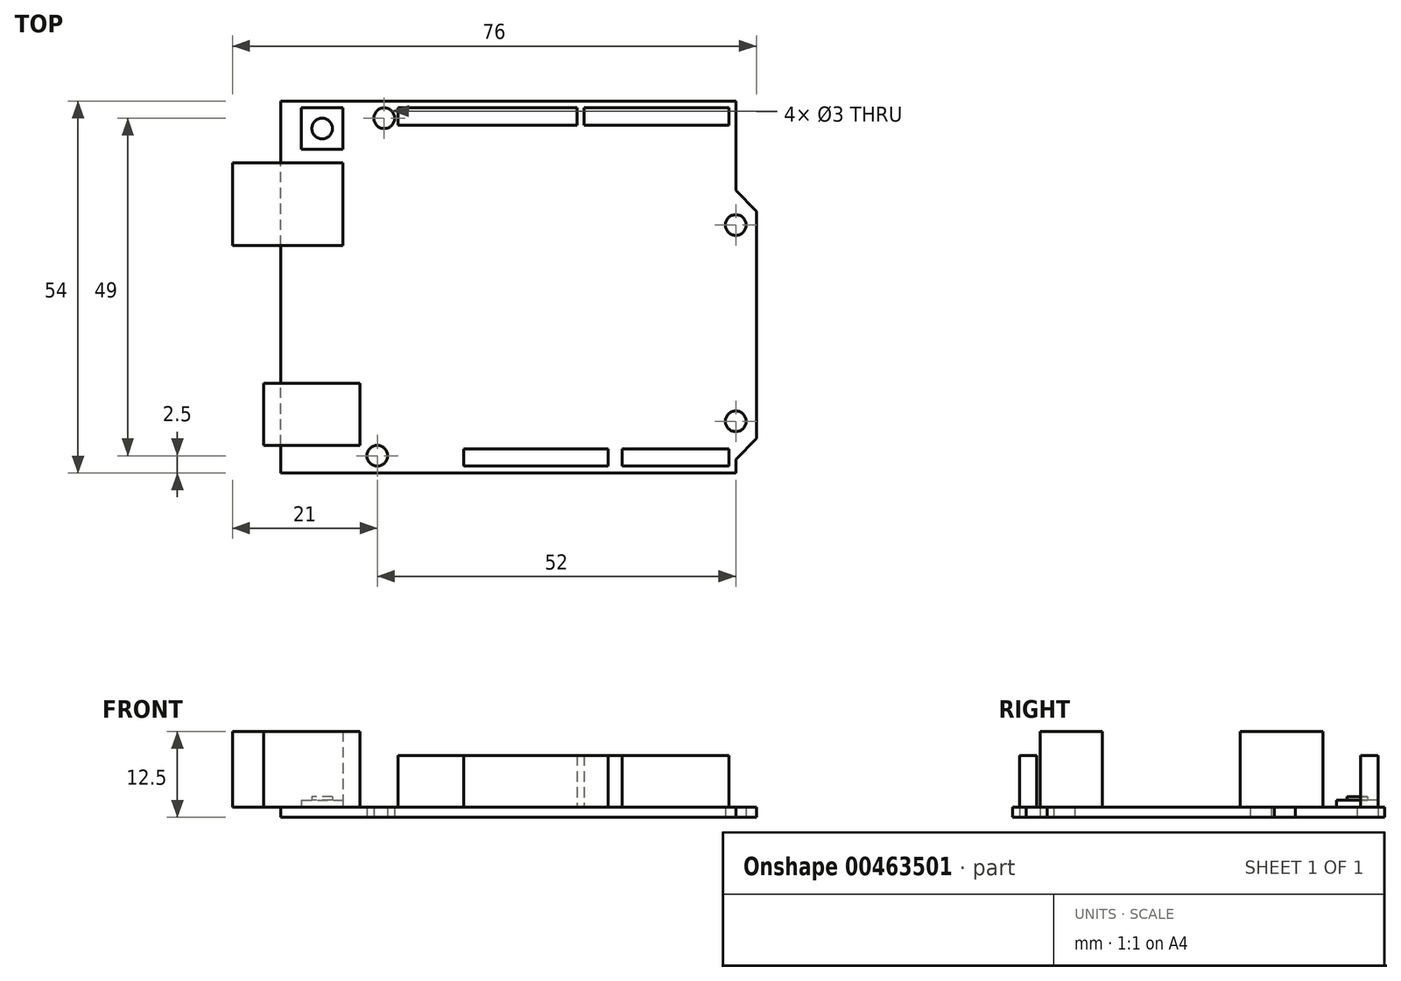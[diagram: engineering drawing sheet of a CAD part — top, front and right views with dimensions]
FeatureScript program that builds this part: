
annotation { "Feature Type Name" : "Feature", "Feature Type Description" : "" }
export const myFeature = defineFeature(function(context is Context, id is Id, definition is map)
    precondition{}
    {
        {
            var Q0;
            Q0=qCreatedBy(makeId("Top.planeOp"),FACE);
            var sketch = newSketch(context, id + "F0", { "sketchPlane" : qUnion([Q0])});
            skLineSegment(sketch, "E0.bottom", {"start": v(-33, 27) * mm, "end": v(33, 27) * mm});
            skLineSegment(sketch, "E0.top", {"start": v(-33, -27) * mm, "end": v(33, -27) * mm});
            skLineSegment(sketch, "E0.left", {"start": v(-33, 27) * mm, "end": v(-33, -27) * mm});
            skLineSegment(sketch, "E0.right", {"start": v(33, 27) * mm, "end": v(33, -27) * mm});
            skLineSegment(sketch, "E1", {"start": v(33, 14) * mm, "end": v(36, 11) * mm});
            skLineSegment(sketch, "E2", {"start": v(36, 11) * mm, "end": v(36, -22) * mm});
            skLineSegment(sketch, "E3", {"start": v(36, -22) * mm, "end": v(33, -25) * mm});
            skCircle(sketch, "E4", {"center": v(33, -19.5) * mm, "radius": 1.5 * mm});
            skCircle(sketch, "E5", {"center": v(-19, -24.5) * mm, "radius": 1.5 * mm});
            skCircle(sketch, "E6", {"center": v(-18, 24.5) * mm, "radius": 1.5 * mm});
            skCircle(sketch, "E7", {"center": v(33, 9) * mm, "radius": 1.5 * mm});
            skLineSegment(sketch, "E8.bottom", {"start": v(-40, 18) * mm, "end": v(-24, 18) * mm});
            skLineSegment(sketch, "E8.top", {"start": v(-40, 6) * mm, "end": v(-24, 6) * mm});
            skLineSegment(sketch, "E8.left", {"start": v(-40, 18) * mm, "end": v(-40, 6) * mm});
            skLineSegment(sketch, "E8.right", {"start": v(-24, 18) * mm, "end": v(-24, 6) * mm});
            skLineSegment(sketch, "E9.bottom", {"start": v(-35.5, -14) * mm, "end": v(-21.5, -14) * mm});
            skLineSegment(sketch, "E9.top", {"start": v(-35.5, -23) * mm, "end": v(-21.5, -23) * mm});
            skLineSegment(sketch, "E9.left", {"start": v(-35.5, -14) * mm, "end": v(-35.5, -23) * mm});
            skLineSegment(sketch, "E9.right", {"start": v(-21.5, -14) * mm, "end": v(-21.5, -23) * mm});
            skLineSegment(sketch, "E10.bottom", {"start": v(-30, 26) * mm, "end": v(-24, 26) * mm});
            skLineSegment(sketch, "E10.top", {"start": v(-30, 20) * mm, "end": v(-24, 20) * mm});
            skLineSegment(sketch, "E10.left", {"start": v(-30, 26) * mm, "end": v(-30, 20) * mm});
            skLineSegment(sketch, "E10.right", {"start": v(-24, 26) * mm, "end": v(-24, 20) * mm});
            skLineSegment(sketch, "E11.bottom", {"start": v(16.5, -23.5) * mm, "end": v(32, -23.5) * mm});
            skLineSegment(sketch, "E11.top", {"start": v(16.5, -26) * mm, "end": v(32, -26) * mm});
            skLineSegment(sketch, "E11.left", {"start": v(16.5, -23.5) * mm, "end": v(16.5, -26) * mm});
            skLineSegment(sketch, "E11.right", {"start": v(32, -23.5) * mm, "end": v(32, -26) * mm});
            skLineSegment(sketch, "E12.bottom", {"start": v(11, 26) * mm, "end": v(32, 26) * mm});
            skLineSegment(sketch, "E12.top", {"start": v(11, 23.5) * mm, "end": v(32, 23.5) * mm});
            skLineSegment(sketch, "E12.left", {"start": v(11, 26) * mm, "end": v(11, 23.5) * mm});
            skLineSegment(sketch, "E12.right", {"start": v(32, 26) * mm, "end": v(32, 23.5) * mm});
            skLineSegment(sketch, "E13.bottom", {"start": v(-16, 26) * mm, "end": v(10, 26) * mm});
            skLineSegment(sketch, "E13.top", {"start": v(-16, 23.5) * mm, "end": v(10, 23.5) * mm});
            skLineSegment(sketch, "E13.left", {"start": v(-16, 26) * mm, "end": v(-16, 23.5) * mm});
            skLineSegment(sketch, "E13.right", {"start": v(10, 26) * mm, "end": v(10, 23.5) * mm});
            skLineSegment(sketch, "E14.bottom", {"start": v(14.5, -23.5) * mm, "end": v(-6.5, -23.5) * mm});
            skLineSegment(sketch, "E14.top", {"start": v(14.5, -26) * mm, "end": v(-6.5, -26) * mm});
            skLineSegment(sketch, "E14.left", {"start": v(14.5, -23.5) * mm, "end": v(14.5, -26) * mm});
            skLineSegment(sketch, "E14.right", {"start": v(-6.5, -23.5) * mm, "end": v(-6.5, -26) * mm});
            skCircle(sketch, "E15", {"center": v(-27, 23) * mm, "radius": 1.5 * mm});
            skSolve(sketch);
        }
        {
            var Q0;
            {var subQ16=sQuery(id+"F0.wireOp",EDGE,"E0.bottom");Q0=makeQuery(id+"F0.imprint","IMPRINT",FACE,{"disambiguationData":[TD([[makeQuery(id+"F0.imprint","IMPRINT",EDGE,{"derivedFrom":subQ16}),-1.0]])]});}
            var Q1;
            {var subQ0=sQuery(id+"F0.wireOp",EDGE,"E1");Q1=makeQuery(id+"F0.imprint","IMPRINT",FACE,{"disambiguationData":[TD([[makeQuery(id+"F0.imprint","IMPRINT",EDGE,{"derivedFrom":subQ0}),-1.0]])]});}
            extrude(context, id + "F1", {"entities" : qUnion([Q0, Q1]), "depth" : 1.5 * mm});
        }
        {
            var Q0;
            Q0=makeQuery(id+"F0.imprint","IMPRINT",FACE,{"disambiguationData":[TD([[makeQuery(id+"F0.imprint","IMPRINT",EDGE,{"derivedFrom":sQuery(id+"F0.wireOp",EDGE,"E13.bottom")}),-1.0]])]});
            var Q1;
            Q1=makeQuery(id+"F0.imprint","IMPRINT",FACE,{"disambiguationData":[TD([[makeQuery(id+"F0.imprint","IMPRINT",EDGE,{"derivedFrom":sQuery(id+"F0.wireOp",EDGE,"E12.bottom")}),-1.0]])]});
            var Q2;
            Q2=makeQuery(id+"F0.imprint","IMPRINT",FACE,{"disambiguationData":[TD([[makeQuery(id+"F0.imprint","IMPRINT",EDGE,{"derivedFrom":sQuery(id+"F0.wireOp",EDGE,"E14.bottom")}),1.0]])]});
            var Q3;
            Q3=makeQuery(id+"F0.imprint","IMPRINT",FACE,{"disambiguationData":[TD([[makeQuery(id+"F0.imprint","IMPRINT",EDGE,{"derivedFrom":sQuery(id+"F0.wireOp",EDGE,"E11.bottom")}),-1.0]])]});
            extrude(context, id + "F2", {"entities" : qUnion([Q0, Q1, Q2, Q3]), "operationType" : NewBodyOperationType.ADD, "depth" : 9 * mm});
        }
        {
            var Q0;
            Q0=makeQuery(id+"F0.imprint","IMPRINT",FACE,{"disambiguationData":[TD([[makeQuery(id+"F0.imprint","IMPRINT",EDGE,{"derivedFrom":sQuery(id+"F0.wireOp",EDGE,"E10.bottom")}),-1.0]])]});
            extrude(context, id + "F3", {"entities" : qUnion([Q0]), "operationType" : NewBodyOperationType.ADD, "depth" : 2.5 * mm});
        }
        {
            var Q0;
            Q0=makeQuery(id+"F0.imprint","IMPRINT",FACE,{"disambiguationData":[TD([[makeQuery(id+"F0.imprint","IMPRINT",EDGE,{"derivedFrom":sQuery(id+"F0.wireOp",EDGE,"E15")}),1.0]])]});
            extrude(context, id + "F4", {"entities" : qUnion([Q0]), "operationType" : NewBodyOperationType.ADD, "depth" : 3 * mm});
        }
        {
            var Q0;
            {var subQ5=sQuery(id+"F0.wireOp",EDGE,"E8.left");Q0=makeQuery(id+"F0.imprint","IMPRINT",FACE,{"disambiguationData":[TD([[makeQuery(id+"F0.imprint","IMPRINT",EDGE,{"derivedFrom":subQ5}),1.0]])]});}
            var Q1;
            {var subQ5=sQuery(id+"F0.wireOp",EDGE,"E8.right");Q1=makeQuery(id+"F0.imprint","IMPRINT",FACE,{"disambiguationData":[TD([[makeQuery(id+"F0.imprint","IMPRINT",EDGE,{"derivedFrom":subQ5}),-1.0]])]});}
            extrude(context, id + "F5", {"entities" : qUnion([Q0, Q1]), "operationType" : NewBodyOperationType.ADD, "depth" : 12.5 * mm});
        }
        {
            var Q0;
            {var subQ5=sQuery(id+"F0.wireOp",EDGE,"E9.right");Q0=makeQuery(id+"F0.imprint","IMPRINT",FACE,{"disambiguationData":[TD([[makeQuery(id+"F0.imprint","IMPRINT",EDGE,{"derivedFrom":subQ5}),-1.0]])]});}
            var Q1;
            {var subQ5=sQuery(id+"F0.wireOp",EDGE,"E9.left");Q1=makeQuery(id+"F0.imprint","IMPRINT",FACE,{"disambiguationData":[TD([[makeQuery(id+"F0.imprint","IMPRINT",EDGE,{"derivedFrom":subQ5}),1.0]])]});}
            extrude(context, id + "F6", {"entities" : qUnion([Q0, Q1]), "operationType" : NewBodyOperationType.ADD, "depth" : 12.5 * mm});
        }
        {
            var Q0;
            Q0=makeQuery(id+"F5.opExtrude","SWEPT_FACE",FACE,{"disambiguationData":[OSD([sQuery(id+"F0.wireOp",EDGE,"E8.bottom")])]});
            var sketch = newSketch(context, id + "F7", { "sketchPlane" : qUnion([Q0])});
            skLineSegment(sketch, "E16.bottom", {"start": v(33, 1.5) * mm, "end": v(40, 1.5) * mm});
            skLineSegment(sketch, "E16.top", {"start": v(33, 0) * mm, "end": v(40, 0) * mm});
            skLineSegment(sketch, "E16.left", {"start": v(33, 1.5) * mm, "end": v(33, 0) * mm});
            skLineSegment(sketch, "E16.right", {"start": v(40, 1.5) * mm, "end": v(40, 0) * mm});
            skSolve(sketch);
        }
        {
            var Q0;
            Q0=makeQuery(id+"F7.imprint","IMPRINT",FACE,{"disambiguationData":[TD([[makeQuery(id+"F7.imprint","IMPRINT",EDGE,{"derivedFrom":sQuery(id+"F7.wireOp",EDGE,"E16.bottom")}),-1.0]])]});
            extrude(context, id + "F8", {"entities" : qUnion([Q0]), "operationType" : NewBodyOperationType.REMOVE, "endBound" : BoundingType.THROUGH_ALL, "oppositeDirection" : true, "depth" : 44.9 * mm});
        }
    });
